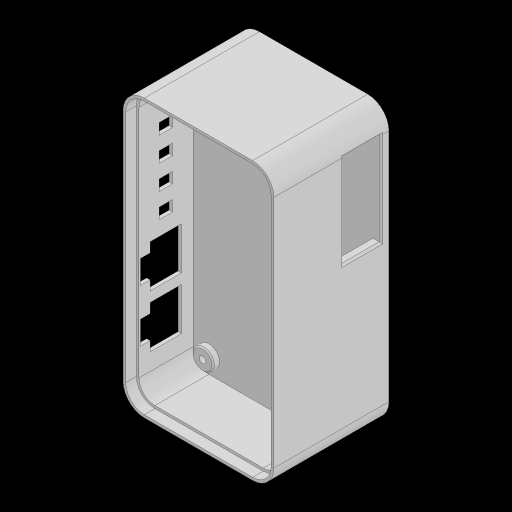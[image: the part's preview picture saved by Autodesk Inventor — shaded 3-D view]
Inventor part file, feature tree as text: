
AUTODESK INVENTOR PART (.ipt)
format: ipt  version: 2024 (Build 280153000, 153)  size: 934,400 bytes
history: native  units: mm
features: sketch x37, extrude x36, projected_geometry x25, chamfer x4, other x3, fillet x3, hole x1, plane x1
ambient origin geometry x8: Origin, YZ Plane, XZ Plane, XY Plane, X Axis, Y Axis, Z Axis, Center Point
bodies: Body1 (feature_tree), Body2 (feature_tree), Body3 (feature_tree)
feature tree (110):
  other  "Main Board"
  extrude  "Extrusion1"  Depth=50.81mm
  hole  "Hole1"  [1 undecoded]
  extrude  "Extrusion2"  Depth=8.0mm
  extrude  "Extrusion3"  Depth=1.65mm
  extrude  "Extrusion4"  Depth=6.6mm
  extrude  "Extrusion5"  Depth=4.0mm
  extrude  "Extrusion6"  Depth=4.0mm
  extrude  "Extrusion7"  Depth=2.0mm TaperAngle=0.0deg
  extrude  "Extrusion8"  Depth=6.0mm
  extrude  "Extrusion9"  Depth=1.7mm
  extrude  "Extrusion10"  Depth=5.6mm TaperAngle=0.0deg
  extrude  "Extrusion11"  Depth=1.6mm TaperAngle=0.0deg
  extrude  "Extrusion12"  Depth=39.3mm
  extrude  "Extrusion13"  Depth=2.86mm
  extrude  "Extrusion14"  Depth=6.0mm TaperAngle=0.0deg
  extrude  "Extrusion15"  Depth=39.3mm
  extrude  "Extrusion16"  Depth=2.84mm
  extrude  "Extrusion17"  Depth=8.4mm
  extrude  "Extrusion18"  Depth=9.2mm
  extrude  "Extrusion19"  Depth=36.43mm
  extrude  "Extrusion20"  Depth=8.0mm
  extrude  "Extrusion21"  Depth=3.75mm
  extrude  "Extrusion22"  Depth=0.08mm
  extrude  "Extrusion23"  Depth=15.91mm
  sketch  "Sketch26"  dims[d67=14.0mm d68=0.0mm d69=0.6mm]
  sketch  "Sketch27"  dims[d70=10.0mm d71=7.82mm d72=12.09mm]
  plane  "Work Plane1"
  extrude  "Extrusion26"  Depth=14.0mm
  extrude  "Extrusion27"  Depth=10.0mm
  fillet  "Fillet2"  Radius=12.09mm
  extrude  "Extrusion29"  Depth=3.73mm
  fillet  "Fillet3"  Radius=3.635mm
  extrude  "Extrusion30"  Depth=16.11mm
  extrude  "Extrusion31"  Depth=14.9mm TaperAngle=0.0deg
  fillet  "Fillet5"  Radius=0.1mm
  extrude  "Extrusion35"  Depth=57.37mm
  chamfer  "Chamfer5"  Distance=2.34mm
  extrude  "Extrusion36"  Depth=1.0mm TaperAngle=0.0deg
  extrude  "Extrusion37"  Depth=24.5mm
  extrude  "Extrusion38"  Depth=0.7mm TaperAngle=0.0deg
  chamfer  "Chamfer6"  Distance=3.0mm
  extrude  "Extrusion39"  Depth=2.0mm
  chamfer  "Chamfer7"  Distance=31.41mm
  extrude  "Extrusion40"  Depth=2.0mm TaperAngle=0.0deg
  extrude  "Extrusion41"  Depth=3.0mm
  chamfer  "Chamfer8"  Distance=12.8mm
  extrude  "Extrusion42"  Depth=35.0mm
  sketch  "Sketch1"  dims[d0=98.33mm d1=50.81mm]
  sketch  "Sketch2"  dims[d2=5.0mm d3=1.54mm d4=0.0mm]
  sketch  "Sketch3"  dims[d5=4.0mm d6=6.0mm d7=4.0mm d8=2.0mm d9=90.0deg d10=8.0mm d11=20.594885mm d12=21.45mm]
  sketch  "Sketch4"  dims[d13=20.1mm d14=1.65mm]
  sketch  "Sketch5"  dims[d15=4.53mm d16=6.6mm]
  sketch  "Sketch6"  dims[d17=4.0mm d18=4.2mm]
  sketch  "Sketch7"  dims[d19=4.0mm d20=4.2mm]
  sketch  "Sketch9"  dims[d22=2.0mm d23=4.6mm d24=0.0mm]
  sketch  "Sketch10"  dims[d25=1.2mm d26=0.0mm d27=6.0mm]
  sketch  "Sketch11"  dims[d28=6.0mm d29=1.7mm]
  sketch  "Sketch12"  dims[d30=15.3mm d31=5.6mm d32=0.0mm]
  sketch  "Sketch13"  dims[d33=3.44mm d34=1.6mm d35=0.0mm]
  projected_geometry  "Projected Loop1"
  projected_geometry  "Projected Loop2"
  sketch  "Sketch14"  dims[d36=17.6mm d37=39.3mm]
  sketch  "Sketch15"  dims[d38=36.46mm d39=2.86mm]
  sketch  "Sketch16"  dims[d40=1.42mm d41=6.0mm d42=0.0mm]
  sketch  "Sketch17"  dims[d43=36.43mm d44=39.3mm]
  sketch  "Sketch18"  dims[d45=1.435mm d46=2.84mm]
  sketch  "Sketch19"  dims[d47=8.4mm d48=0.0mm d49=9.2mm]
  projected_geometry  "Projected Loop3"
  sketch  "Sketch20"  dims[d50=9.2mm d51=9.2mm]
  sketch  "Sketch21"  dims[d53=27.6mm d54=36.43mm]
  sketch  "Sketch22"  dims[d56=4.415mm d57=8.0mm]
  sketch  "Sketch23"  dims[d58=3.75mm d59=0.0mm d60=15.91mm]
  projected_geometry  "Projected Loop4"
  other  "Case"
  sketch  "Sketch24"  dims[d61=16.11mm d62=0.08mm]
  projected_geometry  "Projected Loop5"
  sketch  "Sketch25"  dims[d63=27.55mm d64=15.91mm d65=16.11mm d66=3.71mm]
  projected_geometry  "Projected Loop6"
  projected_geometry  "Projected Loop7"
  projected_geometry  "Projected Loop8"
  projected_geometry  "Projected Loop9"
  projected_geometry  "Projected Loop10"
  projected_geometry  "Projected Loop11"
  projected_geometry  "Projected Loop12"
  sketch  "Sketch28"  dims[d73=4.82mm d74=3.73mm d75=3.635mm]
  projected_geometry  "Projected Loop13"
  other  "Lid"
  sketch  "Sketch29"  dims[d76=2.01mm d77=16.11mm]
  projected_geometry  "Projected Loop14"
  sketch  "Sketch32"  dims[d78=0.05mm]
  projected_geometry  "Projected Loop15"
  projected_geometry  "Projected Loop16"
  sketch  "Sketch34"  dims[d79=7.82mm d80=12.09mm d81=4.82mm d82=3.73mm d83=3.635mm d84=14.9mm d85=0.0mm d86=0.1mm d87=0.0mm]
  projected_geometry  "Projected Loop18"
  sketch  "Sketch35"  dims[d88=2.34mm d89=57.37mm]
  projected_geometry  "Projected Loop19"
  sketch  "Sketch39"  dims[d90=66.48mm]
  projected_geometry  "Projected Loop23"
  sketch  "Sketch40"  dims[d91=3.25mm d92=2.34mm d93=57.37mm d94=22.97mm]
  sketch  "Sketch41"  dims[d95=11.8mm d96=0.0mm d97=1.0mm d98=0.0mm]
  projected_geometry  "Projected Loop24"
  sketch  "Sketch43"  dims[d99=18.0mm d100=24.5mm]
  sketch  "Sketch44"  dims[d101=6.3mm d102=0.7mm d103=0.0mm]
  projected_geometry  "Projected Loop25"
  projected_geometry  "Projected Loop26"
  projected_geometry  "Projected Loop27"
  projected_geometry  "Projected Loop28"
  sketch  "Sketch45"  dims[d104=4.0mm d105=3.0mm d106=6.55mm d107=31.41mm d108=1.9mm d109=0.0mm d110=3.0mm d111=12.8mm d112=35.0mm d113=4.0mm d114=1.9mm d115=0.0mm d116=2.3mm d117=2.3mm d118=0.5mm d119=0.0mm d120=9.0mm d121=3.3mm d122=1.5mm d123=3.7mm d124=9.0mm d125=3.3mm d126=1.5mm d127=2.9mm d128=0.3mm d129=0.3mm d130=7.4mm d131=0.0mm d132=50.0mm d134=2.54mm d135=20.0mm d137=2.54mm d140=2.3mm d141=11.7mm d142=7.4mm d143=0.0mm d144=2.42mm d145=0.0mm d147=1.0mm d148=2.0mm d149=2.0mm d150=0.0mm d151=2.0mm d152=24.36mm d153=0.0mm d154=1.0mm d155=4.0mm d156=0.0mm d157=1.0mm d158=1.0mm d162=7.0mm d163=7.0mm d164=7.0mm d165=7.0mm d174=0.3mm d175=0.8mm d176=10.0mm d177=0.0mm d178=3.0mm d179=0.0mm d180=2.5mm d181=3.5mm d182=3.5mm d190=16.0mm d191=10.0mm d192=0.0mm d193=2.5mm d196=3.0mm d197=14.0mm d198=0.0mm d199=3.0mm d200=0.0mm d201=2.5mm d216=14.0mm d217=35.0mm d218=10.0mm d219=0.0mm d220=0.7mm d221=2.0mm d222=45.0deg d223=45.0deg d224=10.0mm d225=0.0mm d226=10.0mm d227=0.0mm d229=2.0mm d230=2.0mm d231=10.0mm d232=0.0mm d233=0.7mm d234=2.0mm d235=45.0deg d236=1.0mm d237=1.0mm d238=1.0mm d239=1.0mm d240=4.0mm d241=0.0mm d242=0.7mm d243=2.0mm d244=45.0deg d245=2.0mm d246=2.0mm d247=2.0mm d248=2.0mm d249=2.5mm d250=2.5mm d251=2.5mm d252=2.5mm d253=10.0mm d254=0.0mm d255=4.12mm d256=0.0mm d257=0.5mm d258=2.0mm d259=45.0deg d260=0.0mm d261=0.0mm d185=0.5mm d186=0.872665mm d187=0.5mm d188=0.872665mm d204=0.5mm d205=0.872665mm d206=0.5mm d207=0.872665mm d208=0.5mm d209=0.872665mm]
  projected_geometry  "Projected Loop29"
note: 1 required parameter value undecoded (feature->parameter linkage not recoverable at this tier; creation-order binding heuristic only, values carry confidence <= 0.55)
